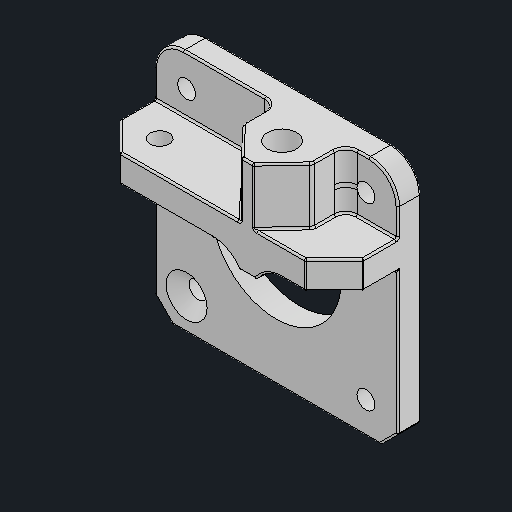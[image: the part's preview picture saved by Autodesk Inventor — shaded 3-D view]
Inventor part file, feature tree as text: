
AUTODESK INVENTOR PART (.ipt)
format: ipt  version: 2024.2 (Build 282272000, 272)  size: 229,888 bytes
history: native  units: mm
features: other x1, fillet x1
ambient origin geometry x8: Origin, YZ Plane, XZ Plane, XY Plane, X Axis, Y Axis, Z Axis, Center Point
bodies: Body1 (feature_tree)
feature tree (2):
  other  "솔리드1"
  fillet  "Fillet6"  [1 undecoded]
note: 1 required parameter value undecoded (feature->parameter linkage not recoverable at this tier; creation-order binding heuristic only, values carry confidence <= 0.55)
